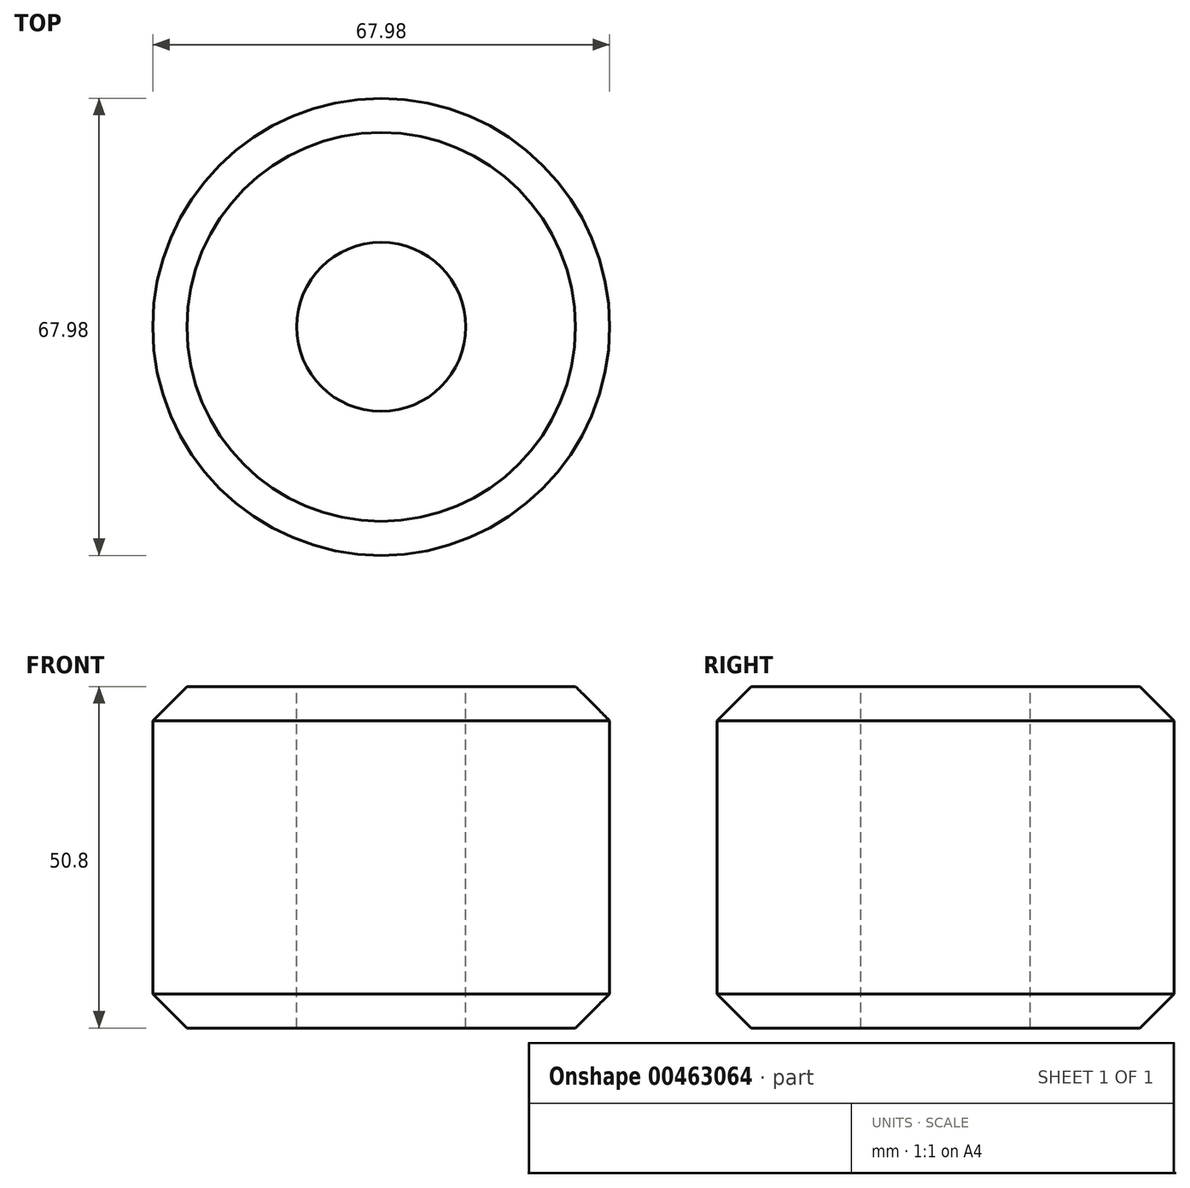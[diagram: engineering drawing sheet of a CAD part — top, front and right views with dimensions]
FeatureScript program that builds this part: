
annotation { "Feature Type Name" : "Feature", "Feature Type Description" : "" }
export const myFeature = defineFeature(function(context is Context, id is Id, definition is map)
    precondition{}
    {
        {
            var Q0;
            Q0=qCreatedBy(makeId("Top.planeOp"),FACE);
            var sketch = newSketch(context, id + "F0", { "sketchPlane" : qUnion([Q0])});
            skCircle(sketch, "E0", {"center": v(0, 0) * mm, "radius": 34 * mm});
            skSolve(sketch);
        }
        {
            var Q0;
            Q0 = qSketchRegion(id + "F0", true);
            extrude(context, id + "F1", {"entities" : qUnion([Q0]), "depth" : 50.8 * mm});
        }
        {
            var Q0;
            Q0=makeQuery(id+"F1.opExtrude","CAP_EDGE",EDGE,{"disambiguationData":[OSD([sQuery(id+"F0.wireOp",EDGE,"E0")])],"isStart":false});
            var Q1;
            Q1=makeQuery(id+"F1.opExtrude","CAP_EDGE",EDGE,{"disambiguationData":[OSD([sQuery(id+"F0.wireOp",EDGE,"E0")])],"isStart":true});
            chamfer(context, id + "F2", {"entities" : qUnion([Q0, Q1]), "width" : 5.08 * mm, "tangentPropagation" : true});
        }
        {
            var Q0;
            Q0=makeQuery(id+"F1.opExtrude","CAP_FACE",FACE,{"disambiguationData":[OSD([sQuery(id+"F0.wireOp",EDGE,"E0")])],"isStart":false});
            var sketch = newSketch(context, id + "F3", { "sketchPlane" : qUnion([Q0])});
            skCircle(sketch, "E1", {"center": v(0, 0) * mm, "radius": 12.58 * mm});
            skSolve(sketch);
        }
        {
            var Q0;
            Q0 = qSketchRegion(id + "F3", true);
            extrude(context, id + "F4", {"entities" : qUnion([Q0]), "operationType" : NewBodyOperationType.REMOVE, "oppositeDirection" : true, "depth" : 76.2 * mm});
        }
    });
